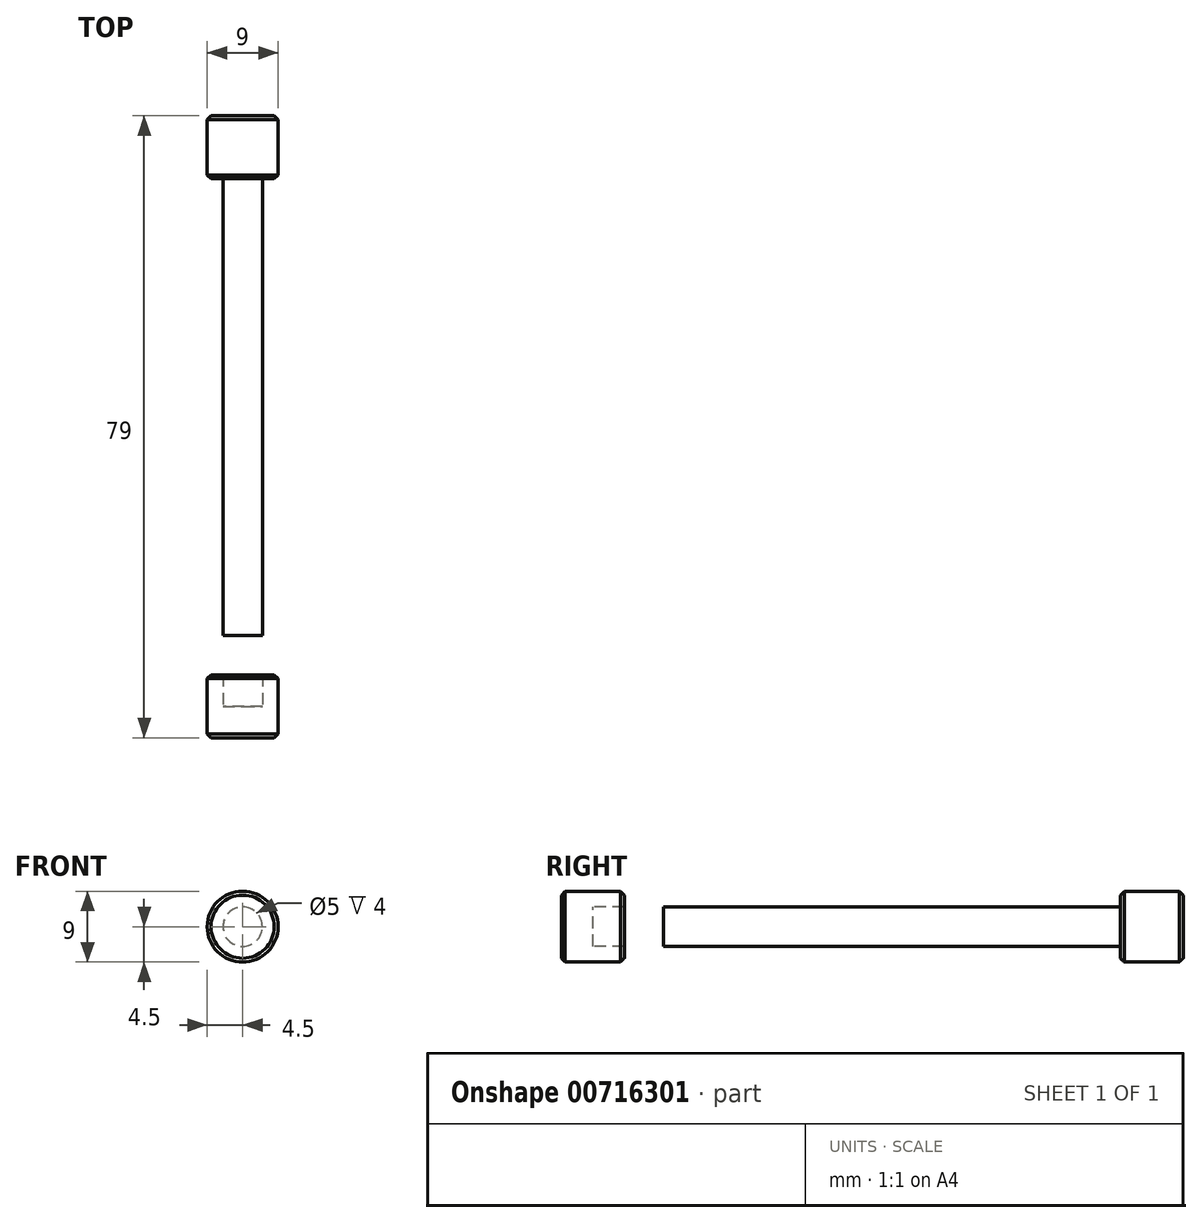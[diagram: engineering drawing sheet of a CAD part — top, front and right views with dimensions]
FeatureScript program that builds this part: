
annotation { "Feature Type Name" : "Feature", "Feature Type Description" : "" }
export const myFeature = defineFeature(function(context is Context, id is Id, definition is map)
    precondition{}
    {
        {
            var Q0;
            Q0=qCreatedBy(makeId("Front.planeOp"),FACE);
            var sketch = newSketch(context, id + "F0", { "sketchPlane" : qUnion([Q0])});
            skCircle(sketch, "E0", {"center": v(0, 0) * mm, "radius": 4.5 * mm});
            skCircle(sketch, "E1", {"center": v(0, 0) * mm, "radius": 2.5 * mm});
            skSolve(sketch);
        }
        {
            var Q0;
            Q0=makeQuery(id+"F0.imprint","IMPRINT",FACE,{"disambiguationData":[TD([[makeQuery(id+"F0.imprint","IMPRINT",EDGE,{"derivedFrom":sQuery(id+"F0.wireOp",EDGE,"E1")}),1.0]])]});
            extrude(context, id + "F1", {"entities" : qUnion([Q0]), "depth" : 58 * mm, "offsetDistance" : 25 * mm});
        }
        {
            var Q0;
            Q0=makeQuery(id+"F0.imprint","IMPRINT",FACE,{"disambiguationData":[TD([[makeQuery(id+"F0.imprint","IMPRINT",EDGE,{"derivedFrom":sQuery(id+"F0.wireOp",EDGE,"E0")}),1.0]])]});
            var Q1;
            Q1=makeQuery(id+"F0.imprint","IMPRINT",FACE,{"disambiguationData":[TD([[makeQuery(id+"F0.imprint","IMPRINT",EDGE,{"derivedFrom":sQuery(id+"F0.wireOp",EDGE,"E1")}),1.0]])]});
            extrude(context, id + "F2", {"entities" : qUnion([Q0, Q1]), "operationType" : NewBodyOperationType.ADD, "oppositeDirection" : true, "depth" : 8 * mm, "offsetDistance" : 25 * mm});
        }
        {
            var Q0;
            Q0=makeQuery(id+"F2.opExtrude","CAP_EDGE",EDGE,{"disambiguationData":[OSD([sQuery(id+"F0.wireOp",EDGE,"E0")])],"isStart":false});
            var Q1;
            Q1=makeQuery(id+"F2.opExtrude","CAP_EDGE",EDGE,{"disambiguationData":[OSD([sQuery(id+"F0.wireOp",EDGE,"E0")])],"isStart":true});
            chamfer(context, id + "F3", {"entities" : qUnion([Q0, Q1]), "width" : 0.5 * mm, "tangentPropagation" : true});
        }
        {
            var Q0;
            Q0=makeQuery(id+"F1.opExtrude","CAP_FACE",FACE,{"disambiguationData":[OSD([sQuery(id+"F0.wireOp",EDGE,"E1")])],"isStart":false});
            cPlane(context, id + "F4", {"entities" : qUnion([Q0]), "cplaneType" : CPlaneType.OFFSET, "offset" : 13 * mm, "width" : 150 * mm, "height" : 150 * mm});
        }
        {
            var Q0;
            Q0=qCreatedBy(id+"F4.planeOp",FACE);
            var sketch = newSketch(context, id + "F5", { "sketchPlane" : qUnion([Q0])});
            skCircle(sketch, "E2", {"center": v(0, 0) * mm, "radius": 4.5 * mm});
            skCircle(sketch, "E3", {"center": v(0, 0) * mm, "radius": 2.5 * mm});
            skSolve(sketch);
        }
        {
            var Q0;
            Q0=makeQuery(id+"F5.imprint","IMPRINT",FACE,{"disambiguationData":[TD([[makeQuery(id+"F5.imprint","IMPRINT",EDGE,{"derivedFrom":sQuery(id+"F5.wireOp",EDGE,"E2")}),1.0]])]});
            extrude(context, id + "F6", {"entities" : qUnion([Q0]), "depth" : -8 * mm, "offsetDistance" : 25 * mm});
        }
        {
            var Q0;
            Q0=makeQuery(id+"F6.opExtrude","CAP_EDGE",EDGE,{"disambiguationData":[OSD([sQuery(id+"F5.wireOp",EDGE,"E2")])],"isStart":false});
            var Q1;
            Q1=makeQuery(id+"F6.opExtrude","CAP_EDGE",EDGE,{"disambiguationData":[OSD([sQuery(id+"F5.wireOp",EDGE,"E2")])],"isStart":true});
            chamfer(context, id + "F7", {"entities" : qUnion([Q0, Q1]), "width" : 0.5 * mm, "tangentPropagation" : true});
        }
        {
            var Q0;
            Q0=makeQuery(id+"F5.imprint","IMPRINT",FACE,{"disambiguationData":[TD([[makeQuery(id+"F5.imprint","IMPRINT",EDGE,{"derivedFrom":sQuery(id+"F5.wireOp",EDGE,"E3")}),1.0]])]});
            extrude(context, id + "F8", {"entities" : qUnion([Q0]), "operationType" : NewBodyOperationType.ADD, "oppositeDirection" : true, "depth" : 4 * mm, "offsetDistance" : 25 * mm});
        }
    });
